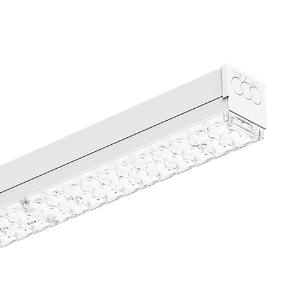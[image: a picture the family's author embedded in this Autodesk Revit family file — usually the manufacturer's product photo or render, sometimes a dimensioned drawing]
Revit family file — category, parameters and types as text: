
# Revit family: 3f_filippi_-_3f_zeta_l_3f_filippi_-_10891_-_3f_zeta_l_50_led_l1783
name_source: partatom
category: Lighting Fixtures
units: mm (PartAtom-declared; Revit-internal decimal feet)

## family parameters
Cut with Voids When Loaded = No
Host = Face
Light Source = No
Part Type = Normal
Room Calculation Point = No
Round Connector Dimension = Use Diameter
Shared = No

## types (1)
- 3F Filippi - 3F Zeta L (1 x LED, 8247 lm, 46 W, 4000 K)
    Apparent Load = 46 VA
    Approval mark = CE
    CIE Flux Codes = 61 95 99 99 100
    Color Rendering = 80
    Color Temperature = 4000 K
    Control Gear = Electronic ballast
    Default Elevation = 1800 mm
    Description = ILLUMINOTECHNICAL
Luminous efficiency 100% (DLOR 99%, ULOR 1%).
Initial luminous flux of the luminaire 8247 lm.
Direct symmetric distribution.
Installation Interdistance Transv.D = 1.39 x hu - Long.D = 1.43 x hu.
Tabular UGR (CIE 117 - 4H-8H; S=0.25H; 70/50/20): RUG 21.7 - 22.4.
Beam angle: 102° - 103°.
Luminous efficacy 179 lm/W.
Lifetime (L93/B10): 30000 h. (tq+25°C)
Lifetime (L90/B10): 50000 h. (tq+25°C)
Lifetime (L85/B10): 80000 h. (tq+25°C)
Lifetime (L80/B10): 100000 h. (tq+25°C)
Sudden decreased luminous flux after 50000 hours: 0% (C0).
Photobiological safety in compliance with IEC/TR 62778: RG0 risk exempt, (IEC 62471).
In compliance with IEC/EN 62722-2-1 - IEC/EN 62717 standards.

SOURCE
Linear LED module 50W/840.
Energy efficiency class (UE 2019/2020 - UE 2019/2015): C.
CIE 13.3 Colour rendering index: CRI >80 (R9 <50%).
IES TM-30 Fidelity Index: Rf = 84 Rg = 95.
CCT nominal colour temperature 4000 K.
Colour initial tolerance (MacAdam): SDCM 3.

MECHANICAL
Housing in hot-galvanised steel, painted in white polyester, obtained through rolling process.
Light unit in hot-galvanised steel, painted in white polyester base with fixing springs and retractable safety hooks in stainless steel.
Lenses for wide distribution, in transparent methacrylate (PMMA) with external flat surface.
End caps in white polycarbonate.
Pair of stainless steel sliding brackets with sliding block screws.
Luminaire with limited surface temperature. - D - (EN 60598-2-24)
Dimensions: 1783x62 mm, height 65 mm. Weight 3.91 kg.
IP40 protection degree.
Mechanical strength to impacts IK06 (1 joule).
Glow-wire test resistance 650°C.

ELECTRICAL
Halogen Free electronic wiring 230V-50/60Hz, power factor 0.95, THD <25%, constant output current, class I, 1 driver.
Power of the luminaire 46 W.
ENEC - CE.
SAFE FLICKER: PstLM=<1 and SVM=<0.4 (IEC TR 61547-1 and IEC TR 63158), to ensure a more comfortable and safe light.
Luminaire compliant with EN 60598-2-22 for power supply from a centralised emergency system CPSS (Central Power Supply System), not incorporated in the luminaire - high risk areas excluded. The default power and flux are 100% in AC and 100% in DC.
Ambient temperature from 0°C to +45°C.
Temperature class T6 max 85°C.
Relative humidity UR: <85%.

INSTALLATION
Ceiling / Suspended / Wall.
All accessories dedicated to this product are available on the Catalog and on our website www.3F-Filippi.com.

APPLICATIONS
Suitable product for food production plants (HACCP), IFS (Food Version 6), BRC (GSFS Food Version 7).
In commercial environments, exhibition areas, shops and stores.

WARNING
Luminaire designed for disposal/recycling at end-of-life.
Replaceable (LED only) light source by a professional. Replaceable control gear by a professional.
    Height = 65 mm
    Lamp = 1 x LED
    Lamp Light Flux = 8247 lm
    Lamp Power = 46 W
    Lamp count = 1
    Length = 1783 mm
    Lifetime = 50000 h
    Luminous efficacy = 179 lm/W
    Manufacturer = 3F Filippi
    ModVariant = No
    Model = 3F Filippi - 10891 - 3F Zeta L 50 LED L1783
    Mounting Place = Ceiling
    Mounting Type = Pendant
    Number of Poles = 1
    OnlyDefault = Yes
    Power Factor = 1
    Product Name = 3F Filippi - 3F Zeta L
    Product group = pendant luminaire
    ProductGroupID = 9
    Protection Class = Protection class I
    Protection Degree = IP 40
    RLX_Detail_Level = 1
    RLX_Emergency_Light_Flux = 0 lm
    RLX_Emergency_Type = 0
    RLX_Emergency_Type_DB = No
    RlxData = <blob elided: 37341 chars, md5=cdb13f51>
    Socket = socket
    Standby Power = 0 W
    System Light Flux = 8247 lm
    System Power = 46 W
    Type Comments = Product without accessories
    Type Image = 3ffilippi_3f_zeta_l.jpg
    URL = http://relux.com
    VarID = ---
    Voltage = 0 V
    Weight = 0.00 kg
    Width = 62 mm  [stored 0.203412 ft]

note: [stored X ft] marks values corroborated as IEEE doubles in the binary element streams (Revit-internal decimal feet)

## geometry (parser evidence)
native form markers: Blend x4, Sweep x9
no freeform markers — native parametric forms only
